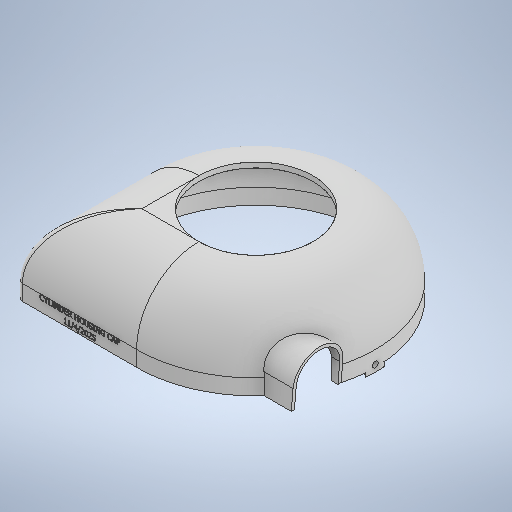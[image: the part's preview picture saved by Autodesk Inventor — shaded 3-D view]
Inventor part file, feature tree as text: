
AUTODESK INVENTOR PART (.ipt)
format: ipt  version: 2025 (Build 290162000, 162)  size: 985,088 bytes
history: native  units: mm
features: sketch x9, extrude x7, fillet x2, projected_geometry x2, hole x1, plane x1, other x1
ambient origin geometry x8: Origin, YZ Plane, XZ Plane, XY Plane, X Axis, Y Axis, Z Axis, Center Point
bodies: Solid1 (feature_tree)
feature tree (23):
  extrude  "Base Shape & Wall"  Depth=5.0mm
  fillet  "Curved Edge"  Radius=75.0mm
  hole  "Cylinder Hole"  [1 undecoded]
  extrude  "Front Tab"  Depth=5.9mm
  extrude  "Bolt Hole"  Depth=4.0mm TaperAngle=0.0deg
  extrude  "Hinge Tab Recess"  Depth=6.5mm
  extrude  "LV Hole"  Depth=15.0mm TaperAngle=0.0deg
  plane  "Work Plane1"
  extrude  "LV Hood"  Depth=53.226mm
  extrude  "Hood Slant Cut"  TaperAngle=0.0deg  [1 undecoded]
  fillet  "Hinge Tab Recess Fillet"  Radius=115.0mm
  other  "LABEL"
  sketch  "Sketch1"  dims[d0=230.0mm d1=5.0mm d2=75.0mm d3=0.0mm]
  sketch  "Sketch2"  dims[d4=60.0mm d5=4.9mm]
  sketch  "Sketch3"  dims[d6=109.9mm d7=6.0mm d8=4.0mm d9=2.0mm d10=90.0deg d11=8.0mm d12=20.594885mm d13=5.9mm]
  projected_geometry  "Projected Loop1"
  sketch  "Sketch4"  dims[d14=8.9mm d15=4.0mm d16=0.0mm]
  sketch  "Sketch5"  dims[d17=5.5mm d18=6.5mm]
  sketch  "Sketch6"  dims[d19=0.0mm d20=0.0mm d23=15.0mm d24=0.0mm]
  sketch  "Sketch8"  dims[d25=42.0mm d26=53.226mm]
  sketch  "Sketch9"  dims[d27=20.0mm d28=0.0mm d29=0.0mm d30=115.0mm]
  projected_geometry  "Projected Loop2"
  sketch  "Sketch10"  dims[d38=3.0mm d39=10.0mm d40=0.0mm d41=10.0mm d42=0.0mm d43=10.1mm d44=3.0mm d45=0.2mm d46=1.0mm d47=0.0mm d34=0.5mm d35=0.872665mm d36=0.5mm d37=0.872665mm]
note: 2 required parameter values undecoded (feature->parameter linkage not recoverable at this tier; creation-order binding heuristic only, values carry confidence <= 0.55)
